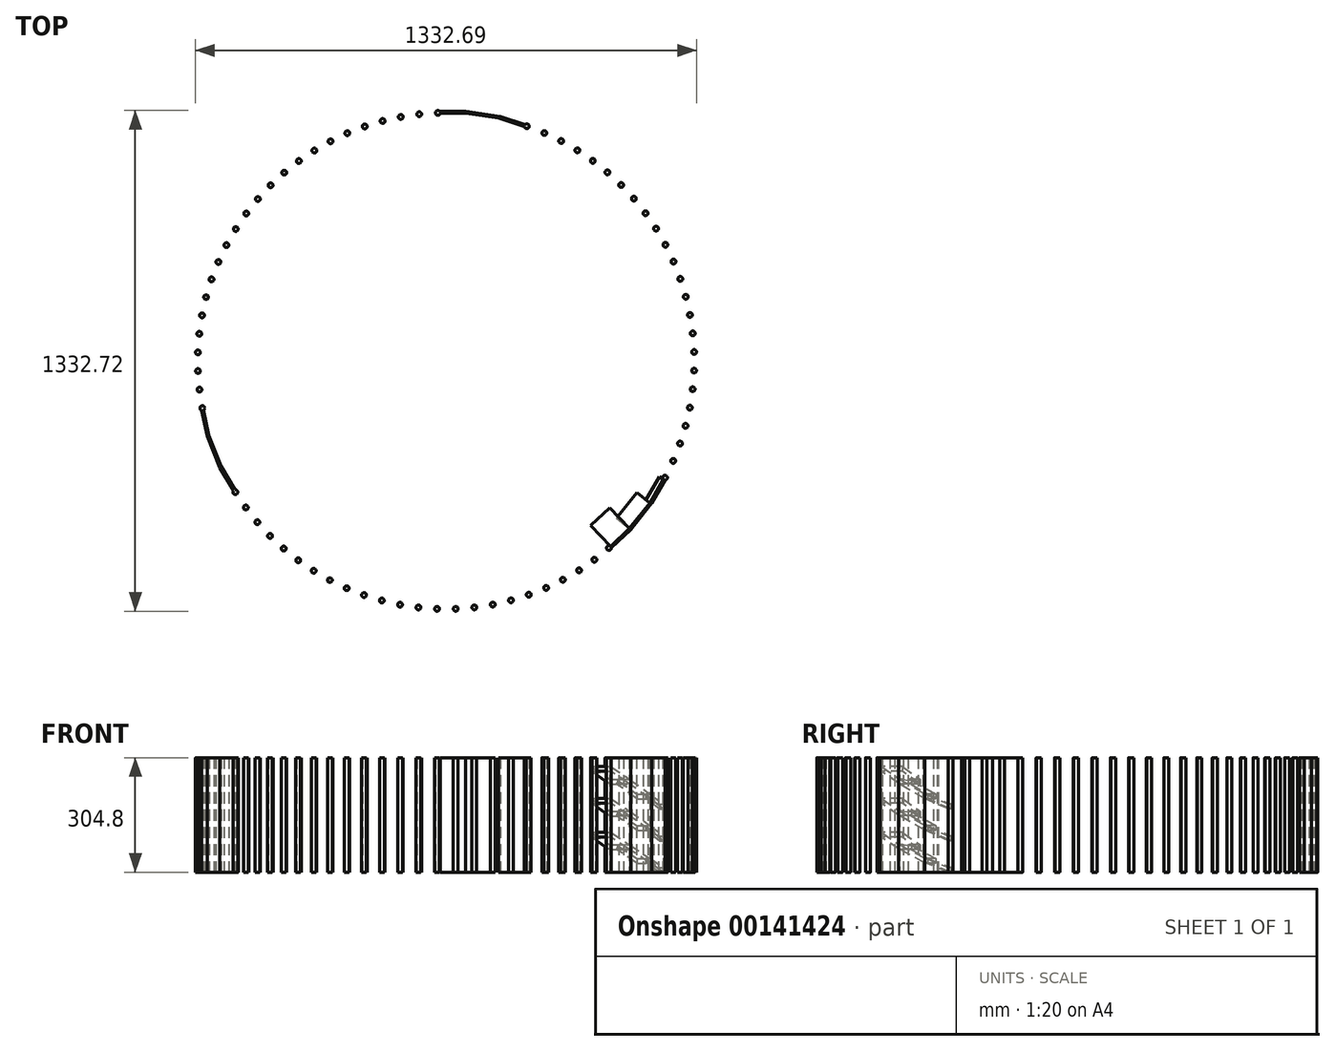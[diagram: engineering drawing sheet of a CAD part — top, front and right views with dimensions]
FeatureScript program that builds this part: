
annotation { "Feature Type Name" : "Feature", "Feature Type Description" : "" }
export const myFeature = defineFeature(function(context is Context, id is Id, definition is map)
    precondition{}
    {
        {
            var Q0;
            Q0=qCreatedBy(makeId("Top.planeOp"),FACE);
            var sketch = newSketch(context, id + "F0", { "sketchPlane" : qUnion([Q0])});
            skCircle(sketch, "E0", {"center": v(-0.04, -0.04) * mm, "radius": 685.8 * mm});
            skCircle(sketch, "E1", {"center": v(-0.04, -0.04) * mm, "radius": 635 * mm});
            skCircle(sketch, "E2", {"center": v(-560.52, -349.32) * mm, "radius": 6.35 * mm});
            skCircle(sketch, "E3", {"center": v(-532.7, -390.43) * mm, "radius": 6.35 * mm});
            skCircle(sketch, "E4", {"center": v(-501.87, -429.34) * mm, "radius": 6.35 * mm});
            skCircle(sketch, "E5", {"center": v(-468.2, -465.83) * mm, "radius": 6.35 * mm});
            skCircle(sketch, "E6", {"center": v(-431.88, -499.69) * mm, "radius": 6.35 * mm});
            skCircle(sketch, "E7", {"center": v(-393.13, -530.71) * mm, "radius": 6.35 * mm});
            skCircle(sketch, "E8", {"center": v(-352.15, -558.74) * mm, "radius": 6.35 * mm});
            skCircle(sketch, "E9", {"center": v(-309.19, -583.62) * mm, "radius": 6.35 * mm});
            skCircle(sketch, "E10", {"center": v(-264.48, -605.19) * mm, "radius": 6.35 * mm});
            skCircle(sketch, "E11", {"center": v(-218.27, -623.34) * mm, "radius": 6.35 * mm});
            skCircle(sketch, "E12", {"center": v(-170.83, -637.98) * mm, "radius": 6.35 * mm});
            skCircle(sketch, "E13", {"center": v(-122.43, -649) * mm, "radius": 6.35 * mm});
            skCircle(sketch, "E14", {"center": v(-73.33, -656.36) * mm, "radius": 6.35 * mm});
            skCircle(sketch, "E15", {"center": v(-23.82, -660.02) * mm, "radius": 6.35 * mm});
            skCircle(sketch, "E16", {"center": v(25.82, -659.94) * mm, "radius": 6.35 * mm});
            skCircle(sketch, "E17", {"center": v(75.32, -656.13) * mm, "radius": 6.35 * mm});
            skCircle(sketch, "E18", {"center": v(124.4, -648.61) * mm, "radius": 6.35 * mm});
            skCircle(sketch, "E19", {"center": v(172.76, -637.43) * mm, "radius": 6.35 * mm});
            skCircle(sketch, "E20", {"center": v(220.15, -622.65) * mm, "radius": 6.35 * mm});
            skCircle(sketch, "E21", {"center": v(266.3, -604.35) * mm, "radius": 6.35 * mm});
            skCircle(sketch, "E22", {"center": v(310.94, -582.64) * mm, "radius": 6.35 * mm});
            skCircle(sketch, "E23", {"center": v(353.83, -557.63) * mm, "radius": 6.35 * mm});
            skCircle(sketch, "E24", {"center": v(582.61, -310.91) * mm, "radius": 6.35 * mm});
            skCircle(sketch, "E25", {"center": v(604.32, -266.26) * mm, "radius": 6.35 * mm});
            skCircle(sketch, "E26", {"center": v(622.61, -220.11) * mm, "radius": 6.35 * mm});
            skCircle(sketch, "E27", {"center": v(637.32, -172.95) * mm, "radius": 6.35 * mm});
            skCircle(sketch, "E28", {"center": v(648.5, -124.59) * mm, "radius": 6.35 * mm});
            skCircle(sketch, "E29", {"center": v(656.03, -75.52) * mm, "radius": 6.35 * mm});
            skCircle(sketch, "E30", {"center": v(659.85, -26.02) * mm, "radius": 6.35 * mm});
            skCircle(sketch, "E31", {"center": v(659.93, 23.62) * mm, "radius": 6.35 * mm});
            skCircle(sketch, "E32", {"center": v(656.3, 73.14) * mm, "radius": 6.35 * mm});
            skCircle(sketch, "E33", {"center": v(648.94, 122.23) * mm, "radius": 6.35 * mm});
            skCircle(sketch, "E34", {"center": v(637.92, 170.64) * mm, "radius": 6.35 * mm});
            skCircle(sketch, "E35", {"center": v(623.3, 218.08) * mm, "radius": 6.35 * mm});
            skCircle(sketch, "E36", {"center": v(605.15, 264.29) * mm, "radius": 6.35 * mm});
            skCircle(sketch, "E37", {"center": v(583.58, 309) * mm, "radius": 6.35 * mm});
            skCircle(sketch, "E38", {"center": v(558.72, 351.97) * mm, "radius": 6.35 * mm});
            skCircle(sketch, "E39", {"center": v(530.7, 392.95) * mm, "radius": 6.35 * mm});
            skCircle(sketch, "E40", {"center": v(499.67, 431.71) * mm, "radius": 6.35 * mm});
            skCircle(sketch, "E41", {"center": v(465.83, 468.03) * mm, "radius": 6.35 * mm});
            skCircle(sketch, "E42", {"center": v(429.35, 501.7) * mm, "radius": 6.35 * mm});
            skCircle(sketch, "E43", {"center": v(390.45, 532.54) * mm, "radius": 6.35 * mm});
            skCircle(sketch, "E44", {"center": v(349.34, 560.37) * mm, "radius": 6.35 * mm});
            skCircle(sketch, "E45", {"center": v(306.25, 585.03) * mm, "radius": 6.35 * mm});
            skCircle(sketch, "E46", {"center": v(-71.28, 656.5) * mm, "radius": 6.35 * mm});
            skCircle(sketch, "E47", {"center": v(-120.4, 649.3) * mm, "radius": 6.35 * mm});
            skCircle(sketch, "E48", {"center": v(-168.84, 638.42) * mm, "radius": 6.35 * mm});
            skCircle(sketch, "E49", {"center": v(-216.32, 623.94) * mm, "radius": 6.35 * mm});
            skCircle(sketch, "E50", {"center": v(-262.59, 605.93) * mm, "radius": 6.35 * mm});
            skCircle(sketch, "E51", {"center": v(-307.36, 584.5) * mm, "radius": 6.35 * mm});
            skCircle(sketch, "E52", {"center": v(-350.4, 559.75) * mm, "radius": 6.35 * mm});
            skCircle(sketch, "E53", {"center": v(-391.47, 531.85) * mm, "radius": 6.35 * mm});
            skCircle(sketch, "E54", {"center": v(-430.32, 500.95) * mm, "radius": 6.35 * mm});
            skCircle(sketch, "E55", {"center": v(-466.74, 467.2) * mm, "radius": 6.35 * mm});
            skCircle(sketch, "E56", {"center": v(-500.52, 430.83) * mm, "radius": 6.35 * mm});
            skCircle(sketch, "E57", {"center": v(-531.47, 392.02) * mm, "radius": 6.35 * mm});
            skCircle(sketch, "E58", {"center": v(-559.42, 350.99) * mm, "radius": 6.35 * mm});
            skCircle(sketch, "E59", {"center": v(-584.21, 307.98) * mm, "radius": 6.35 * mm});
            skCircle(sketch, "E60", {"center": v(-605.7, 263.22) * mm, "radius": 6.35 * mm});
            skCircle(sketch, "E61", {"center": v(-623.76, 216.98) * mm, "radius": 6.35 * mm});
            skCircle(sketch, "E62", {"center": v(-638.3, 169.52) * mm, "radius": 6.35 * mm});
            skCircle(sketch, "E63", {"center": v(-649.24, 121.1) * mm, "radius": 6.35 * mm});
            skCircle(sketch, "E64", {"center": v(-656.5, 71.98) * mm, "radius": 6.35 * mm});
            skCircle(sketch, "E65", {"center": v(-660.06, 22.46) * mm, "radius": 6.35 * mm});
            skCircle(sketch, "E66", {"center": v(-659.89, -27.18) * mm, "radius": 6.35 * mm});
            skCircle(sketch, "E67", {"center": v(-655.98, -76.67) * mm, "radius": 6.35 * mm});
            skCircle(sketch, "E68", {"center": v(-648.37, -125.73) * mm, "radius": 6.35 * mm});
            skCircle(sketch, "E69", {"center": v(394.72, -529.47) * mm, "radius": 6.35 * mm});
            skCircle(sketch, "E70", {"center": v(261.43, 606.39) * mm, "radius": 6.35 * mm});
            skCircle(sketch, "E71", {"center": v(-21.76, 660) * mm, "radius": 6.35 * mm});
            skCircle(sketch, "E72", {"center": v(433.37, -498.32) * mm, "radius": 6.35 * mm});
            skCircle(sketch, "E73", {"center": v(215.14, 624.32) * mm, "radius": 6.35 * mm});
            skLineSegment(sketch, "E74", {"start": v(-650, -131.25) * mm, "end": v(-634.8, -201.04) * mm});
            skLineSegment(sketch, "E75", {"start": v(-634.8, -201.04) * mm, "end": v(-602, -284.28) * mm});
            skLineSegment(sketch, "E76", {"start": v(-602, -284.28) * mm, "end": v(-565.87, -345.9) * mm});
            skLineSegment(sketch, "E77", {"start": v(-645.23, -131.25) * mm, "end": v(-630.68, -198.61) * mm});
            skLineSegment(sketch, "E78", {"start": v(-630.68, -198.61) * mm, "end": v(-598.55, -280.98) * mm});
            skLineSegment(sketch, "E79", {"start": v(-598.55, -280.98) * mm, "end": v(-561.97, -343.13) * mm});
            skLineSegment(sketch, "E80", {"start": v(439.72, -498.32) * mm, "end": v(491.69, -449.09) * mm});
            skLineSegment(sketch, "E81", {"start": v(491.69, -449.09) * mm, "end": v(547.14, -379.06) * mm});
            skLineSegment(sketch, "E82", {"start": v(582.61, -317.26) * mm, "end": v(547.14, -379.06) * mm});
            skLineSegment(sketch, "E83", {"start": v(437.93, -493.9) * mm, "end": v(487.86, -446.23) * mm});
            skLineSegment(sketch, "E84", {"start": v(578.29, -315.56) * mm, "end": v(542.51, -377.89) * mm});
            skLineSegment(sketch, "E85", {"start": v(542.51, -377.89) * mm, "end": v(487.86, -446.23) * mm});
            skLineSegment(sketch, "E86", {"start": v(-16.6, 663.7) * mm, "end": v(53.34, 663.7) * mm});
            skLineSegment(sketch, "E87", {"start": v(141.74, 650.55) * mm, "end": v(210.48, 628.63) * mm});
            skLineSegment(sketch, "E88", {"start": v(53.34, 663.7) * mm, "end": v(144.24, 649.75) * mm});
            skLineSegment(sketch, "E89", {"start": v(-15.48, 659.05) * mm, "end": v(52.23, 659.05) * mm});
            skLineSegment(sketch, "E90", {"start": v(52.23, 659.05) * mm, "end": v(139.9, 646.14) * mm});
            skLineSegment(sketch, "E91", {"start": v(139.9, 646.14) * mm, "end": v(208.8, 624.17) * mm});
            skSolve(sketch);
        }
        {
            var Q0;
            {var subQ0=sQuery(id+"F0.wireOp",EDGE,"E2");var subQ1=makeQuery(id+"F0.imprint","INTERSECT",VERTEX,{"derivedFrom":[subQ0,sQuery(id+"F0.wireOp",EDGE,"E76")]});Q0=makeQuery(id+"F0.imprint","IMPRINT",FACE,{"disambiguationData":[TD([[makeQuery(id+"F0.imprint","IMPRINT",EDGE,{"disambiguationData":[TD([[subQ1,1.0]])],"derivedFrom":subQ0}),1.0]])]});}
            var Q1;
            {var subQ0=sQuery(id+"F0.wireOp",EDGE,"E75");Q1=makeQuery(id+"F0.imprint","IMPRINT",FACE,{"disambiguationData":[TD([[makeQuery(id+"F0.imprint","IMPRINT",EDGE,{"derivedFrom":subQ0}),1.0]])]});}
            var Q2;
            {var subQ0=sQuery(id+"F0.wireOp",EDGE,"E68");var subQ1=makeQuery(id+"F0.imprint","INTERSECT",VERTEX,{"derivedFrom":[subQ0,sQuery(id+"F0.wireOp",EDGE,"E77")]});Q2=makeQuery(id+"F0.imprint","IMPRINT",FACE,{"disambiguationData":[TD([[makeQuery(id+"F0.imprint","IMPRINT",EDGE,{"disambiguationData":[TD([[subQ1,1.0]])],"derivedFrom":subQ0}),1.0]])]});}
            var Q3;
            Q3=makeQuery(id+"F0.imprint","IMPRINT",FACE,{"disambiguationData":[TD([[makeQuery(id+"F0.imprint","IMPRINT",EDGE,{"derivedFrom":sQuery(id+"F0.wireOp",EDGE,"E62")}),1.0]])]});
            var Q4;
            Q4=makeQuery(id+"F0.imprint","IMPRINT",FACE,{"disambiguationData":[TD([[makeQuery(id+"F0.imprint","IMPRINT",EDGE,{"derivedFrom":sQuery(id+"F0.wireOp",EDGE,"E63")}),1.0]])]});
            var Q5;
            Q5=makeQuery(id+"F0.imprint","IMPRINT",FACE,{"disambiguationData":[TD([[makeQuery(id+"F0.imprint","IMPRINT",EDGE,{"derivedFrom":sQuery(id+"F0.wireOp",EDGE,"E64")}),1.0]])]});
            var Q6;
            Q6=makeQuery(id+"F0.imprint","IMPRINT",FACE,{"disambiguationData":[TD([[makeQuery(id+"F0.imprint","IMPRINT",EDGE,{"derivedFrom":sQuery(id+"F0.wireOp",EDGE,"E65")}),1.0]])]});
            var Q7;
            Q7=makeQuery(id+"F0.imprint","IMPRINT",FACE,{"disambiguationData":[TD([[makeQuery(id+"F0.imprint","IMPRINT",EDGE,{"derivedFrom":sQuery(id+"F0.wireOp",EDGE,"E66")}),1.0]])]});
            var Q8;
            Q8=makeQuery(id+"F0.imprint","IMPRINT",FACE,{"disambiguationData":[TD([[makeQuery(id+"F0.imprint","IMPRINT",EDGE,{"derivedFrom":sQuery(id+"F0.wireOp",EDGE,"E67")}),1.0]])]});
            var Q9;
            Q9=makeQuery(id+"F0.imprint","IMPRINT",FACE,{"disambiguationData":[TD([[makeQuery(id+"F0.imprint","IMPRINT",EDGE,{"derivedFrom":sQuery(id+"F0.wireOp",EDGE,"E61")}),1.0]])]});
            var Q10;
            Q10=makeQuery(id+"F0.imprint","IMPRINT",FACE,{"disambiguationData":[TD([[makeQuery(id+"F0.imprint","IMPRINT",EDGE,{"derivedFrom":sQuery(id+"F0.wireOp",EDGE,"E60")}),1.0]])]});
            var Q11;
            Q11=makeQuery(id+"F0.imprint","IMPRINT",FACE,{"disambiguationData":[TD([[makeQuery(id+"F0.imprint","IMPRINT",EDGE,{"derivedFrom":sQuery(id+"F0.wireOp",EDGE,"E59")}),1.0]])]});
            var Q12;
            Q12=makeQuery(id+"F0.imprint","IMPRINT",FACE,{"disambiguationData":[TD([[makeQuery(id+"F0.imprint","IMPRINT",EDGE,{"derivedFrom":sQuery(id+"F0.wireOp",EDGE,"E58")}),1.0]])]});
            var Q13;
            Q13=makeQuery(id+"F0.imprint","IMPRINT",FACE,{"disambiguationData":[TD([[makeQuery(id+"F0.imprint","IMPRINT",EDGE,{"derivedFrom":sQuery(id+"F0.wireOp",EDGE,"E57")}),1.0]])]});
            var Q14;
            Q14=makeQuery(id+"F0.imprint","IMPRINT",FACE,{"disambiguationData":[TD([[makeQuery(id+"F0.imprint","IMPRINT",EDGE,{"derivedFrom":sQuery(id+"F0.wireOp",EDGE,"E56")}),1.0]])]});
            var Q15;
            Q15=makeQuery(id+"F0.imprint","IMPRINT",FACE,{"disambiguationData":[TD([[makeQuery(id+"F0.imprint","IMPRINT",EDGE,{"derivedFrom":sQuery(id+"F0.wireOp",EDGE,"E55")}),1.0]])]});
            var Q16;
            Q16=makeQuery(id+"F0.imprint","IMPRINT",FACE,{"disambiguationData":[TD([[makeQuery(id+"F0.imprint","IMPRINT",EDGE,{"derivedFrom":sQuery(id+"F0.wireOp",EDGE,"E54")}),1.0]])]});
            var Q17;
            Q17=makeQuery(id+"F0.imprint","IMPRINT",FACE,{"disambiguationData":[TD([[makeQuery(id+"F0.imprint","IMPRINT",EDGE,{"derivedFrom":sQuery(id+"F0.wireOp",EDGE,"E53")}),1.0]])]});
            var Q18;
            Q18=makeQuery(id+"F0.imprint","IMPRINT",FACE,{"disambiguationData":[TD([[makeQuery(id+"F0.imprint","IMPRINT",EDGE,{"derivedFrom":sQuery(id+"F0.wireOp",EDGE,"E52")}),1.0]])]});
            var Q19;
            Q19=makeQuery(id+"F0.imprint","IMPRINT",FACE,{"disambiguationData":[TD([[makeQuery(id+"F0.imprint","IMPRINT",EDGE,{"derivedFrom":sQuery(id+"F0.wireOp",EDGE,"E51")}),1.0]])]});
            var Q20;
            Q20=makeQuery(id+"F0.imprint","IMPRINT",FACE,{"disambiguationData":[TD([[makeQuery(id+"F0.imprint","IMPRINT",EDGE,{"derivedFrom":sQuery(id+"F0.wireOp",EDGE,"E50")}),1.0]])]});
            var Q21;
            Q21=makeQuery(id+"F0.imprint","IMPRINT",FACE,{"disambiguationData":[TD([[makeQuery(id+"F0.imprint","IMPRINT",EDGE,{"derivedFrom":sQuery(id+"F0.wireOp",EDGE,"E49")}),1.0]])]});
            var Q22;
            Q22=makeQuery(id+"F0.imprint","IMPRINT",FACE,{"disambiguationData":[TD([[makeQuery(id+"F0.imprint","IMPRINT",EDGE,{"derivedFrom":sQuery(id+"F0.wireOp",EDGE,"E48")}),1.0]])]});
            var Q23;
            Q23=makeQuery(id+"F0.imprint","IMPRINT",FACE,{"disambiguationData":[TD([[makeQuery(id+"F0.imprint","IMPRINT",EDGE,{"derivedFrom":sQuery(id+"F0.wireOp",EDGE,"E47")}),1.0]])]});
            var Q24;
            Q24=makeQuery(id+"F0.imprint","IMPRINT",FACE,{"disambiguationData":[TD([[makeQuery(id+"F0.imprint","IMPRINT",EDGE,{"derivedFrom":sQuery(id+"F0.wireOp",EDGE,"E46")}),1.0]])]});
            var Q25;
            {var subQ0=sQuery(id+"F0.wireOp",EDGE,"E71");var subQ1=makeQuery(id+"F0.imprint","INTERSECT",VERTEX,{"derivedFrom":[subQ0,sQuery(id+"F0.wireOp",EDGE,"E86")]});Q25=makeQuery(id+"F0.imprint","IMPRINT",FACE,{"disambiguationData":[TD([[makeQuery(id+"F0.imprint","IMPRINT",EDGE,{"disambiguationData":[TD([[subQ1,-1.0]])],"derivedFrom":subQ0}),1.0]])]});}
            var Q26;
            {var subQ4=sQuery(id+"F0.wireOp",EDGE,"E86");Q26=makeQuery(id+"F0.imprint","IMPRINT",FACE,{"disambiguationData":[TD([[makeQuery(id+"F0.imprint","IMPRINT",EDGE,{"derivedFrom":subQ4}),-1.0]])]});}
            var Q27;
            {var subQ0=sQuery(id+"F0.wireOp",EDGE,"E73");var subQ1=makeQuery(id+"F0.imprint","INTERSECT",VERTEX,{"derivedFrom":[subQ0,sQuery(id+"F0.wireOp",EDGE,"E87")]});Q27=makeQuery(id+"F0.imprint","IMPRINT",FACE,{"disambiguationData":[TD([[makeQuery(id+"F0.imprint","IMPRINT",EDGE,{"disambiguationData":[TD([[subQ1,-1.0]])],"derivedFrom":subQ0}),1.0]])]});}
            var Q28;
            Q28=makeQuery(id+"F0.imprint","IMPRINT",FACE,{"disambiguationData":[TD([[makeQuery(id+"F0.imprint","IMPRINT",EDGE,{"derivedFrom":sQuery(id+"F0.wireOp",EDGE,"E70")}),1.0]])]});
            var Q29;
            Q29=makeQuery(id+"F0.imprint","IMPRINT",FACE,{"disambiguationData":[TD([[makeQuery(id+"F0.imprint","IMPRINT",EDGE,{"derivedFrom":sQuery(id+"F0.wireOp",EDGE,"E45")}),1.0]])]});
            var Q30;
            Q30=makeQuery(id+"F0.imprint","IMPRINT",FACE,{"disambiguationData":[TD([[makeQuery(id+"F0.imprint","IMPRINT",EDGE,{"derivedFrom":sQuery(id+"F0.wireOp",EDGE,"E44")}),1.0]])]});
            var Q31;
            Q31=makeQuery(id+"F0.imprint","IMPRINT",FACE,{"disambiguationData":[TD([[makeQuery(id+"F0.imprint","IMPRINT",EDGE,{"derivedFrom":sQuery(id+"F0.wireOp",EDGE,"E43")}),1.0]])]});
            var Q32;
            Q32=makeQuery(id+"F0.imprint","IMPRINT",FACE,{"disambiguationData":[TD([[makeQuery(id+"F0.imprint","IMPRINT",EDGE,{"derivedFrom":sQuery(id+"F0.wireOp",EDGE,"E42")}),1.0]])]});
            var Q33;
            Q33=makeQuery(id+"F0.imprint","IMPRINT",FACE,{"disambiguationData":[TD([[makeQuery(id+"F0.imprint","IMPRINT",EDGE,{"derivedFrom":sQuery(id+"F0.wireOp",EDGE,"E41")}),1.0]])]});
            var Q34;
            Q34=makeQuery(id+"F0.imprint","IMPRINT",FACE,{"disambiguationData":[TD([[makeQuery(id+"F0.imprint","IMPRINT",EDGE,{"derivedFrom":sQuery(id+"F0.wireOp",EDGE,"E40")}),1.0]])]});
            var Q35;
            Q35=makeQuery(id+"F0.imprint","IMPRINT",FACE,{"disambiguationData":[TD([[makeQuery(id+"F0.imprint","IMPRINT",EDGE,{"derivedFrom":sQuery(id+"F0.wireOp",EDGE,"E39")}),1.0]])]});
            var Q36;
            Q36=makeQuery(id+"F0.imprint","IMPRINT",FACE,{"disambiguationData":[TD([[makeQuery(id+"F0.imprint","IMPRINT",EDGE,{"derivedFrom":sQuery(id+"F0.wireOp",EDGE,"E38")}),1.0]])]});
            var Q37;
            Q37=makeQuery(id+"F0.imprint","IMPRINT",FACE,{"disambiguationData":[TD([[makeQuery(id+"F0.imprint","IMPRINT",EDGE,{"derivedFrom":sQuery(id+"F0.wireOp",EDGE,"E37")}),1.0]])]});
            var Q38;
            Q38=makeQuery(id+"F0.imprint","IMPRINT",FACE,{"disambiguationData":[TD([[makeQuery(id+"F0.imprint","IMPRINT",EDGE,{"derivedFrom":sQuery(id+"F0.wireOp",EDGE,"E36")}),1.0]])]});
            var Q39;
            Q39=makeQuery(id+"F0.imprint","IMPRINT",FACE,{"disambiguationData":[TD([[makeQuery(id+"F0.imprint","IMPRINT",EDGE,{"derivedFrom":sQuery(id+"F0.wireOp",EDGE,"E35")}),1.0]])]});
            var Q40;
            Q40=makeQuery(id+"F0.imprint","IMPRINT",FACE,{"disambiguationData":[TD([[makeQuery(id+"F0.imprint","IMPRINT",EDGE,{"derivedFrom":sQuery(id+"F0.wireOp",EDGE,"E34")}),1.0]])]});
            var Q41;
            Q41=makeQuery(id+"F0.imprint","IMPRINT",FACE,{"disambiguationData":[TD([[makeQuery(id+"F0.imprint","IMPRINT",EDGE,{"derivedFrom":sQuery(id+"F0.wireOp",EDGE,"E33")}),1.0]])]});
            var Q42;
            Q42=makeQuery(id+"F0.imprint","IMPRINT",FACE,{"disambiguationData":[TD([[makeQuery(id+"F0.imprint","IMPRINT",EDGE,{"derivedFrom":sQuery(id+"F0.wireOp",EDGE,"E32")}),1.0]])]});
            var Q43;
            Q43=makeQuery(id+"F0.imprint","IMPRINT",FACE,{"disambiguationData":[TD([[makeQuery(id+"F0.imprint","IMPRINT",EDGE,{"derivedFrom":sQuery(id+"F0.wireOp",EDGE,"E31")}),1.0]])]});
            var Q44;
            Q44=makeQuery(id+"F0.imprint","IMPRINT",FACE,{"disambiguationData":[TD([[makeQuery(id+"F0.imprint","IMPRINT",EDGE,{"derivedFrom":sQuery(id+"F0.wireOp",EDGE,"E30")}),1.0]])]});
            var Q45;
            Q45=makeQuery(id+"F0.imprint","IMPRINT",FACE,{"disambiguationData":[TD([[makeQuery(id+"F0.imprint","IMPRINT",EDGE,{"derivedFrom":sQuery(id+"F0.wireOp",EDGE,"E29")}),1.0]])]});
            var Q46;
            Q46=makeQuery(id+"F0.imprint","IMPRINT",FACE,{"disambiguationData":[TD([[makeQuery(id+"F0.imprint","IMPRINT",EDGE,{"derivedFrom":sQuery(id+"F0.wireOp",EDGE,"E28")}),1.0]])]});
            var Q47;
            Q47=makeQuery(id+"F0.imprint","IMPRINT",FACE,{"disambiguationData":[TD([[makeQuery(id+"F0.imprint","IMPRINT",EDGE,{"derivedFrom":sQuery(id+"F0.wireOp",EDGE,"E27")}),1.0]])]});
            var Q48;
            Q48=makeQuery(id+"F0.imprint","IMPRINT",FACE,{"disambiguationData":[TD([[makeQuery(id+"F0.imprint","IMPRINT",EDGE,{"derivedFrom":sQuery(id+"F0.wireOp",EDGE,"E26")}),1.0]])]});
            var Q49;
            Q49=makeQuery(id+"F0.imprint","IMPRINT",FACE,{"disambiguationData":[TD([[makeQuery(id+"F0.imprint","IMPRINT",EDGE,{"derivedFrom":sQuery(id+"F0.wireOp",EDGE,"E25")}),1.0]])]});
            var Q50;
            {var subQ0=sQuery(id+"F0.wireOp",EDGE,"E24");var subQ1=makeQuery(id+"F0.imprint","INTERSECT",VERTEX,{"derivedFrom":[subQ0,sQuery(id+"F0.wireOp",EDGE,"E82")]});Q50=makeQuery(id+"F0.imprint","IMPRINT",FACE,{"disambiguationData":[TD([[makeQuery(id+"F0.imprint","IMPRINT",EDGE,{"disambiguationData":[TD([[subQ1,1.0]])],"derivedFrom":subQ0}),1.0]])]});}
            var Q51;
            {var subQ0=sQuery(id+"F0.wireOp",EDGE,"E80");Q51=makeQuery(id+"F0.imprint","IMPRINT",FACE,{"disambiguationData":[TD([[makeQuery(id+"F0.imprint","IMPRINT",EDGE,{"derivedFrom":subQ0}),1.0]])]});}
            var Q52;
            {var subQ0=sQuery(id+"F0.wireOp",EDGE,"E72");var subQ1=makeQuery(id+"F0.imprint","INTERSECT",VERTEX,{"derivedFrom":[subQ0,sQuery(id+"F0.wireOp",EDGE,"E80")]});Q52=makeQuery(id+"F0.imprint","IMPRINT",FACE,{"disambiguationData":[TD([[makeQuery(id+"F0.imprint","IMPRINT",EDGE,{"disambiguationData":[TD([[subQ1,-1.0]])],"derivedFrom":subQ0}),1.0]])]});}
            var Q53;
            Q53=makeQuery(id+"F0.imprint","IMPRINT",FACE,{"disambiguationData":[TD([[makeQuery(id+"F0.imprint","IMPRINT",EDGE,{"derivedFrom":sQuery(id+"F0.wireOp",EDGE,"E3")}),1.0]])]});
            var Q54;
            Q54=makeQuery(id+"F0.imprint","IMPRINT",FACE,{"disambiguationData":[TD([[makeQuery(id+"F0.imprint","IMPRINT",EDGE,{"derivedFrom":sQuery(id+"F0.wireOp",EDGE,"E4")}),1.0]])]});
            var Q55;
            Q55=makeQuery(id+"F0.imprint","IMPRINT",FACE,{"disambiguationData":[TD([[makeQuery(id+"F0.imprint","IMPRINT",EDGE,{"derivedFrom":sQuery(id+"F0.wireOp",EDGE,"E5")}),1.0]])]});
            var Q56;
            Q56=makeQuery(id+"F0.imprint","IMPRINT",FACE,{"disambiguationData":[TD([[makeQuery(id+"F0.imprint","IMPRINT",EDGE,{"derivedFrom":sQuery(id+"F0.wireOp",EDGE,"E6")}),1.0]])]});
            var Q57;
            Q57=makeQuery(id+"F0.imprint","IMPRINT",FACE,{"disambiguationData":[TD([[makeQuery(id+"F0.imprint","IMPRINT",EDGE,{"derivedFrom":sQuery(id+"F0.wireOp",EDGE,"E7")}),1.0]])]});
            var Q58;
            Q58=makeQuery(id+"F0.imprint","IMPRINT",FACE,{"disambiguationData":[TD([[makeQuery(id+"F0.imprint","IMPRINT",EDGE,{"derivedFrom":sQuery(id+"F0.wireOp",EDGE,"E8")}),1.0]])]});
            var Q59;
            Q59=makeQuery(id+"F0.imprint","IMPRINT",FACE,{"disambiguationData":[TD([[makeQuery(id+"F0.imprint","IMPRINT",EDGE,{"derivedFrom":sQuery(id+"F0.wireOp",EDGE,"E9")}),1.0]])]});
            var Q60;
            Q60=makeQuery(id+"F0.imprint","IMPRINT",FACE,{"disambiguationData":[TD([[makeQuery(id+"F0.imprint","IMPRINT",EDGE,{"derivedFrom":sQuery(id+"F0.wireOp",EDGE,"E10")}),1.0]])]});
            var Q61;
            Q61=makeQuery(id+"F0.imprint","IMPRINT",FACE,{"disambiguationData":[TD([[makeQuery(id+"F0.imprint","IMPRINT",EDGE,{"derivedFrom":sQuery(id+"F0.wireOp",EDGE,"E11")}),1.0]])]});
            var Q62;
            Q62=makeQuery(id+"F0.imprint","IMPRINT",FACE,{"disambiguationData":[TD([[makeQuery(id+"F0.imprint","IMPRINT",EDGE,{"derivedFrom":sQuery(id+"F0.wireOp",EDGE,"E12")}),1.0]])]});
            var Q63;
            Q63=makeQuery(id+"F0.imprint","IMPRINT",FACE,{"disambiguationData":[TD([[makeQuery(id+"F0.imprint","IMPRINT",EDGE,{"derivedFrom":sQuery(id+"F0.wireOp",EDGE,"E13")}),1.0]])]});
            var Q64;
            Q64=makeQuery(id+"F0.imprint","IMPRINT",FACE,{"disambiguationData":[TD([[makeQuery(id+"F0.imprint","IMPRINT",EDGE,{"derivedFrom":sQuery(id+"F0.wireOp",EDGE,"E14")}),1.0]])]});
            var Q65;
            Q65=makeQuery(id+"F0.imprint","IMPRINT",FACE,{"disambiguationData":[TD([[makeQuery(id+"F0.imprint","IMPRINT",EDGE,{"derivedFrom":sQuery(id+"F0.wireOp",EDGE,"E15")}),1.0]])]});
            var Q66;
            Q66=makeQuery(id+"F0.imprint","IMPRINT",FACE,{"disambiguationData":[TD([[makeQuery(id+"F0.imprint","IMPRINT",EDGE,{"derivedFrom":sQuery(id+"F0.wireOp",EDGE,"E16")}),1.0]])]});
            var Q67;
            Q67=makeQuery(id+"F0.imprint","IMPRINT",FACE,{"disambiguationData":[TD([[makeQuery(id+"F0.imprint","IMPRINT",EDGE,{"derivedFrom":sQuery(id+"F0.wireOp",EDGE,"E17")}),1.0]])]});
            var Q68;
            Q68=makeQuery(id+"F0.imprint","IMPRINT",FACE,{"disambiguationData":[TD([[makeQuery(id+"F0.imprint","IMPRINT",EDGE,{"derivedFrom":sQuery(id+"F0.wireOp",EDGE,"E18")}),1.0]])]});
            var Q69;
            Q69=makeQuery(id+"F0.imprint","IMPRINT",FACE,{"disambiguationData":[TD([[makeQuery(id+"F0.imprint","IMPRINT",EDGE,{"derivedFrom":sQuery(id+"F0.wireOp",EDGE,"E19")}),1.0]])]});
            var Q70;
            Q70=makeQuery(id+"F0.imprint","IMPRINT",FACE,{"disambiguationData":[TD([[makeQuery(id+"F0.imprint","IMPRINT",EDGE,{"derivedFrom":sQuery(id+"F0.wireOp",EDGE,"E20")}),1.0]])]});
            var Q71;
            Q71=makeQuery(id+"F0.imprint","IMPRINT",FACE,{"disambiguationData":[TD([[makeQuery(id+"F0.imprint","IMPRINT",EDGE,{"derivedFrom":sQuery(id+"F0.wireOp",EDGE,"E21")}),1.0]])]});
            var Q72;
            Q72=makeQuery(id+"F0.imprint","IMPRINT",FACE,{"disambiguationData":[TD([[makeQuery(id+"F0.imprint","IMPRINT",EDGE,{"derivedFrom":sQuery(id+"F0.wireOp",EDGE,"E22")}),1.0]])]});
            var Q73;
            Q73=makeQuery(id+"F0.imprint","IMPRINT",FACE,{"disambiguationData":[TD([[makeQuery(id+"F0.imprint","IMPRINT",EDGE,{"derivedFrom":sQuery(id+"F0.wireOp",EDGE,"E23")}),1.0]])]});
            var Q74;
            Q74=makeQuery(id+"F0.imprint","IMPRINT",FACE,{"disambiguationData":[TD([[makeQuery(id+"F0.imprint","IMPRINT",EDGE,{"derivedFrom":sQuery(id+"F0.wireOp",EDGE,"E69")}),1.0]])]});
            extrude(context, id + "F1", {"entities" : qUnion([Q0, Q1, Q2, Q3, Q4, Q5, Q6, Q7, Q8, Q9, Q10, Q11, Q12, Q13, Q14, Q15, Q16, Q17, Q18, Q19, Q20, Q21, Q22, Q23, Q24, Q25, Q26, Q27, Q28, Q29, Q30, Q31, Q32, Q33, Q34, Q35, Q36, Q37, Q38, Q39, Q40, Q41, Q42, Q43, Q44, Q45, Q46, Q47, Q48, Q49, Q50, Q51, Q52, Q53, Q54, Q55, Q56, Q57, Q58, Q59, Q60, Q61, Q62, Q63, Q64, Q65, Q66, Q67, Q68, Q69, Q70, Q71, Q72, Q73, Q74]), "depth" : 304.8 * mm});
        }
        {
            var Q0;
            Q0=makeQuery(id+"F1.opExtrude","SWEPT_FACE",FACE,{"disambiguationData":[OSD([sQuery(id+"F0.wireOp",EDGE,"E84")])]});
            var sketch = newSketch(context, id + "F2", { "sketchPlane" : qUnion([Q0])});
            skLineSegment(sketch, "E92", {"start": v(-14.18, 0) * mm, "end": v(198.8, 73.06) * mm});
            skLineSegment(sketch, "E93", {"start": v(198.8, 73.06) * mm, "end": v(198.8, 85.76) * mm});
            skLineSegment(sketch, "E94", {"start": v(198.8, 85.76) * mm, "end": v(-14.18, 12.7) * mm});
            skLineSegment(sketch, "E95", {"start": v(-14.18, 12.7) * mm, "end": v(-14.18, 0) * mm});
            skLineSegment(sketch, "E96", {"start": v(199.79, 262.2) * mm, "end": v(-14.18, 180.75) * mm});
            skLineSegment(sketch, "E97", {"start": v(-14.18, 180.75) * mm, "end": v(-14.18, 168.05) * mm});
            skLineSegment(sketch, "E98", {"start": v(-14.18, 168.05) * mm, "end": v(198.79, 249.54) * mm});
            skLineSegment(sketch, "E99", {"start": v(198.79, 249.54) * mm, "end": v(199.79, 262.2) * mm});
            skLineSegment(sketch, "E100", {"start": v(-14.18, 84.03) * mm, "end": v(198.72, 164.4) * mm});
            skLineSegment(sketch, "E101", {"start": v(198.72, 164.4) * mm, "end": v(198.72, 177.1) * mm});
            skLineSegment(sketch, "E102", {"start": v(198.72, 177.1) * mm, "end": v(-14.18, 96.73) * mm});
            skLineSegment(sketch, "E103", {"start": v(-14.18, 96.73) * mm, "end": v(-14.18, 84.03) * mm});
            skSolve(sketch);
        }
        {
            var Q0;
            Q0=makeQuery(id+"F1.opExtrude","SWEPT_FACE",FACE,{"disambiguationData":[OSD([sQuery(id+"F0.wireOp",EDGE,"E85")])]});
            var sketch = newSketch(context, id + "F3", { "sketchPlane" : qUnion([Q0])});
            skLineSegment(sketch, "E104", {"start": v(-43.7, 24.4) * mm, "end": v(43.82, 61.11) * mm});
            skLineSegment(sketch, "E105", {"start": v(43.82, 61.11) * mm, "end": v(43.82, 73.81) * mm});
            skLineSegment(sketch, "E106", {"start": v(43.82, 73.81) * mm, "end": v(-43.7, 37.1) * mm});
            skLineSegment(sketch, "E107", {"start": v(-43.7, 37.1) * mm, "end": v(-43.7, 24.4) * mm});
            skLineSegment(sketch, "E108", {"start": v(-43.7, 111.15) * mm, "end": v(43.82, 150.53) * mm});
            skLineSegment(sketch, "E109", {"start": v(43.82, 150.53) * mm, "end": v(43.82, 163.23) * mm});
            skLineSegment(sketch, "E110", {"start": v(43.82, 163.23) * mm, "end": v(-43.7, 123.85) * mm});
            skLineSegment(sketch, "E111", {"start": v(-43.7, 123.85) * mm, "end": v(-43.7, 111.15) * mm});
            skLineSegment(sketch, "E112", {"start": v(-43.7, 208.36) * mm, "end": v(-43.7, 195.66) * mm});
            skLineSegment(sketch, "E113", {"start": v(-43.7, 195.66) * mm, "end": v(43.82, 235.11) * mm});
            skLineSegment(sketch, "E114", {"start": v(43.82, 235.11) * mm, "end": v(43.82, 247.81) * mm});
            skLineSegment(sketch, "E115", {"start": v(43.82, 247.81) * mm, "end": v(-43.7, 208.36) * mm});
            skSolve(sketch);
        }
        {
            var Q0;
            Q0=makeQuery(id+"F1.opExtrude","SWEPT_FACE",FACE,{"disambiguationData":[OSD([sQuery(id+"F0.wireOp",EDGE,"E83")])]});
            var sketch = newSketch(context, id + "F4", { "sketchPlane" : qUnion([Q0])});
            skLineSegment(sketch, "E116", {"start": v(-44.8, 73.3) * mm, "end": v(-44.8, 60.6) * mm});
            skLineSegment(sketch, "E117", {"start": v(-44.8, 60.6) * mm, "end": v(24.23, 93.26) * mm});
            skLineSegment(sketch, "E118", {"start": v(24.23, 93.26) * mm, "end": v(24.23, 105.96) * mm});
            skLineSegment(sketch, "E119", {"start": v(24.23, 105.96) * mm, "end": v(-44.8, 73.3) * mm});
            skLineSegment(sketch, "E120", {"start": v(-44.8, 150.12) * mm, "end": v(24.23, 184.06) * mm});
            skLineSegment(sketch, "E121", {"start": v(24.23, 184.06) * mm, "end": v(24.23, 196.76) * mm});
            skLineSegment(sketch, "E122", {"start": v(24.23, 196.76) * mm, "end": v(-44.8, 162.82) * mm});
            skLineSegment(sketch, "E123", {"start": v(-44.8, 162.82) * mm, "end": v(-44.8, 150.12) * mm});
            skLineSegment(sketch, "E124", {"start": v(-44.8, 235.04) * mm, "end": v(24.23, 268.88) * mm});
            skLineSegment(sketch, "E125", {"start": v(24.23, 268.88) * mm, "end": v(24.23, 281.58) * mm});
            skLineSegment(sketch, "E126", {"start": v(24.23, 281.58) * mm, "end": v(-44.8, 247.74) * mm});
            skLineSegment(sketch, "E127", {"start": v(-44.8, 247.74) * mm, "end": v(-44.8, 235.04) * mm});
            skSolve(sketch);
        }
        {
            var Q0;
            {var subQ0=sQuery(id+"F2.wireOp",EDGE,"E95");Q0=makeQuery(id+"F2.imprint","IMPRINT",FACE,{"disambiguationData":[TD([[makeQuery(id+"F2.imprint","IMPRINT",EDGE,{"derivedFrom":subQ0}),1.0]])]});}
            var Q1;
            {var subQ0=sQuery(id+"F2.wireOp",EDGE,"E103");Q1=makeQuery(id+"F2.imprint","IMPRINT",FACE,{"disambiguationData":[TD([[makeQuery(id+"F2.imprint","IMPRINT",EDGE,{"derivedFrom":subQ0}),1.0]])]});}
            var Q2;
            {var subQ0=sQuery(id+"F2.wireOp",EDGE,"E97");Q2=makeQuery(id+"F2.imprint","IMPRINT",FACE,{"disambiguationData":[TD([[makeQuery(id+"F2.imprint","IMPRINT",EDGE,{"derivedFrom":subQ0}),1.0]])]});}
            extrude(context, id + "F5", {"entities" : qUnion([Q0, Q1, Q2]), "operationType" : NewBodyOperationType.ADD, "depth" : 12.7 * mm});
        }
        {
            var Q0;
            Q0=makeQuery(id+"F3.imprint","IMPRINT",FACE,{"disambiguationData":[TD([[makeQuery(id+"F3.imprint","IMPRINT",EDGE,{"derivedFrom":sQuery(id+"F3.wireOp",EDGE,"E104")}),1.0]])]});
            var Q1;
            Q1=makeQuery(id+"F3.imprint","IMPRINT",FACE,{"disambiguationData":[TD([[makeQuery(id+"F3.imprint","IMPRINT",EDGE,{"derivedFrom":sQuery(id+"F3.wireOp",EDGE,"E108")}),1.0]])]});
            var Q2;
            Q2=makeQuery(id+"F3.imprint","IMPRINT",FACE,{"disambiguationData":[TD([[makeQuery(id+"F3.imprint","IMPRINT",EDGE,{"derivedFrom":sQuery(id+"F3.wireOp",EDGE,"E112")}),1.0]])]});
            extrude(context, id + "F6", {"entities" : qUnion([Q0, Q1, Q2]), "operationType" : NewBodyOperationType.ADD, "depth" : 44.45 * mm});
        }
        {
            var Q0;
            Q0=makeQuery(id+"F4.imprint","IMPRINT",FACE,{"disambiguationData":[TD([[makeQuery(id+"F4.imprint","IMPRINT",EDGE,{"derivedFrom":sQuery(id+"F4.wireOp",EDGE,"E116")}),1.0]])]});
            var Q1;
            Q1=makeQuery(id+"F4.imprint","IMPRINT",FACE,{"disambiguationData":[TD([[makeQuery(id+"F4.imprint","IMPRINT",EDGE,{"derivedFrom":sQuery(id+"F4.wireOp",EDGE,"E120")}),1.0]])]});
            var Q2;
            Q2=makeQuery(id+"F4.imprint","IMPRINT",FACE,{"disambiguationData":[TD([[makeQuery(id+"F4.imprint","IMPRINT",EDGE,{"derivedFrom":sQuery(id+"F4.wireOp",EDGE,"E124")}),1.0]])]});
            extrude(context, id + "F7", {"entities" : qUnion([Q0, Q1, Q2]), "operationType" : NewBodyOperationType.ADD, "depth" : 76.2 * mm});
        }
    });
